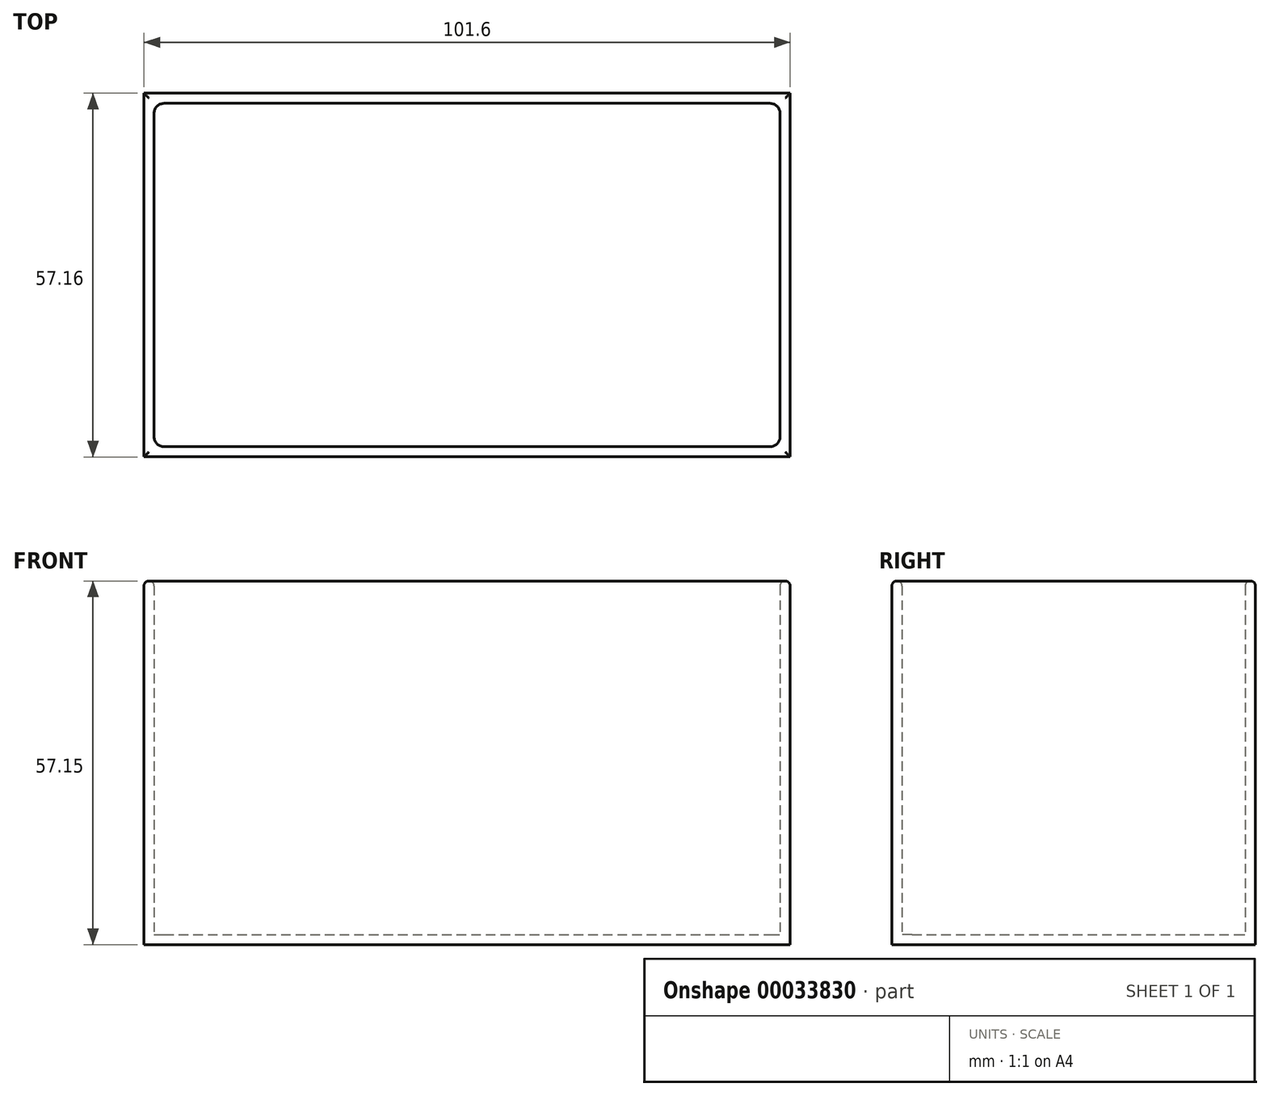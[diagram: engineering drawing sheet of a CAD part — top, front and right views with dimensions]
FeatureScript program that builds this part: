
annotation { "Feature Type Name" : "Feature", "Feature Type Description" : "" }
export const myFeature = defineFeature(function(context is Context, id is Id, definition is map)
    precondition{}
    {
        {
            var Q0;
            Q0=qCreatedBy(makeId("Top.planeOp"),FACE);
            var sketch = newSketch(context, id + "F0", { "sketchPlane" : qUnion([Q0])});
            skLineSegment(sketch, "E0.rect.bottom", {"start": v(50.8, -28.58) * mm, "end": v(-50.8, -28.58) * mm});
            skLineSegment(sketch, "E0.rect.top", {"start": v(50.8, 28.58) * mm, "end": v(-50.8, 28.57) * mm});
            skLineSegment(sketch, "E0.rect.left", {"start": v(50.8, -28.58) * mm, "end": v(50.8, 28.58) * mm});
            skLineSegment(sketch, "E0.rect.right", {"start": v(-50.8, -28.58) * mm, "end": v(-50.8, 28.57) * mm});
            skPoint(sketch, "E0.rect.middle", {"position": v(0, 0) * mm});
            skLineSegment(sketch, "E1.rect.bottom", {"start": v(-49.21, -26.99) * mm, "end": v(49.21, -26.99) * mm});
            skLineSegment(sketch, "E1.rect.top", {"start": v(-49.21, 26.99) * mm, "end": v(49.21, 26.99) * mm});
            skLineSegment(sketch, "E1.rect.left", {"start": v(-49.21, -26.99) * mm, "end": v(-49.21, 26.99) * mm});
            skLineSegment(sketch, "E1.rect.right", {"start": v(49.21, -26.99) * mm, "end": v(49.21, 26.99) * mm});
            skSolve(sketch);
        }
        {
            var Q0;
            Q0=makeQuery(id+"F0.imprint","IMPRINT",FACE,{"disambiguationData":[TD([[makeQuery(id+"F0.imprint","IMPRINT",EDGE,{"derivedFrom":sQuery(id+"F0.wireOp",EDGE,"E0.rect.bottom")}),-1.0]])]});
            extrude(context, id + "F1", {"entities" : qUnion([Q0]), "depth" : 57.15 * mm});
        }
        {
            var Q0;
            Q0=makeQuery(id+"F0.imprint","IMPRINT",FACE,{"disambiguationData":[TD([[makeQuery(id+"F0.imprint","IMPRINT",EDGE,{"derivedFrom":sQuery(id+"F0.wireOp",EDGE,"E1.rect.bottom")}),1.0]])]});
            extrude(context, id + "F2", {"entities" : qUnion([Q0]), "operationType" : NewBodyOperationType.ADD, "depth" : 1.59 * mm});
        }
        {
            var Q0;
            Q0=makeQuery(id+"F1.opExtrude","SWEPT_EDGE",EDGE,{"disambiguationData":[OSD([sQuery(id+"F0.wireOp",EDGE,"E1.rect.top"),sQuery(id+"F0.wireOp",EDGE,"E1.rect.left")])]});
            var Q1;
            Q1=makeQuery(id+"F1.opExtrude","SWEPT_EDGE",EDGE,{"disambiguationData":[OSD([sQuery(id+"F0.wireOp",EDGE,"E1.rect.top"),sQuery(id+"F0.wireOp",EDGE,"E1.rect.right")])]});
            var Q2;
            Q2=makeQuery(id+"F1.opExtrude","SWEPT_EDGE",EDGE,{"disambiguationData":[OSD([sQuery(id+"F0.wireOp",EDGE,"E1.rect.bottom"),sQuery(id+"F0.wireOp",EDGE,"E1.rect.right")])]});
            var Q3;
            Q3=makeQuery(id+"F2.opExtrude","CAP_EDGE",EDGE,{"disambiguationData":[OSD([sQuery(id+"F0.wireOp",EDGE,"E1.rect.right")])],"isStart":false});
            var Q4;
            Q4=makeQuery(id+"F2.opExtrude","CAP_EDGE",EDGE,{"disambiguationData":[OSD([sQuery(id+"F0.wireOp",EDGE,"E1.rect.bottom")])],"isStart":false});
            var Q5;
            Q5=makeQuery(id+"F2.opExtrude","CAP_EDGE",EDGE,{"disambiguationData":[OSD([sQuery(id+"F0.wireOp",EDGE,"E1.rect.left")])],"isStart":false});
            var Q6;
            Q6=makeQuery(id+"F2.opExtrude","CAP_EDGE",EDGE,{"disambiguationData":[OSD([sQuery(id+"F0.wireOp",EDGE,"E1.rect.top")])],"isStart":false});
            var Q7;
            Q7=makeQuery(id+"F1.opExtrude","SWEPT_EDGE",EDGE,{"disambiguationData":[OSD([sQuery(id+"F0.wireOp",EDGE,"E1.rect.bottom"),sQuery(id+"F0.wireOp",EDGE,"E1.rect.left")])]});
            fillet(context, id + "F3", {"entities" : qUnion([Q0, Q1, Q2, Q3, Q4, Q5, Q6, Q7]), "radius" : 1.57 * mm, "tangentPropagation" : true, "allowEdgeOverflow" : false});
        }
        {
            var Q0;
            Q0=makeQuery(id+"F1.opExtrude","CAP_EDGE",EDGE,{"disambiguationData":[OSD([sQuery(id+"F0.wireOp",EDGE,"E0.rect.bottom")])],"isStart":false});
            var Q1;
            Q1=makeQuery(id+"F1.opExtrude","CAP_EDGE",EDGE,{"disambiguationData":[OSD([sQuery(id+"F0.wireOp",EDGE,"E0.rect.left")])],"isStart":false});
            var Q2;
            Q2=makeQuery(id+"F1.opExtrude","CAP_EDGE",EDGE,{"disambiguationData":[OSD([sQuery(id+"F0.wireOp",EDGE,"E0.rect.top")])],"isStart":false});
            var Q3;
            Q3=makeQuery(id+"F1.opExtrude","CAP_EDGE",EDGE,{"disambiguationData":[OSD([sQuery(id+"F0.wireOp",EDGE,"E0.rect.right")])],"isStart":false});
            var Q4;
            Q4=makeQuery(id+"F1.opExtrude","CAP_EDGE",EDGE,{"disambiguationData":[OSD([sQuery(id+"F0.wireOp",EDGE,"E1.rect.left")])],"isStart":false});
            fillet(context, id + "F4", {"entities" : qUnion([Q0, Q1, Q2, Q3, Q4]), "radius" : 0.76 * mm, "tangentPropagation" : true, "allowEdgeOverflow" : false});
        }
        {
            var Q0;
            Q0=qCreatedBy(makeId("Front.planeOp"),FACE);
            var sketch = newSketch(context, id + "F5", { "sketchPlane" : qUnion([Q0])});
            skCircle(sketch, "E2", {"center": v(-50.14, -40.55) * mm, "radius": 20.64 * mm});
            skSolve(sketch);
        }
        {
            var Q0;
            Q0=makeQuery(id+"F5.imprint","IMPRINT",FACE,{"disambiguationData":[TD([[makeQuery(id+"F5.imprint","IMPRINT",EDGE,{"derivedFrom":sQuery(id+"F5.wireOp",EDGE,"E2")}),1.0]])]});
            extrude(context, id + "F6", {"entities" : qUnion([Q0]), "depth" : 6.35 * mm});
        }
        {
            var Q0;
            Q0=makeQuery(id+"F6.opExtrude","SWEPT_BODY",BODY,{"disambiguationData":[OSD([sQuery(id+"F5.wireOp",EDGE,"E2")])]});
            deleteBodies(context, id + "F7", {"entities" : qUnion([Q0])});
        }
    });
